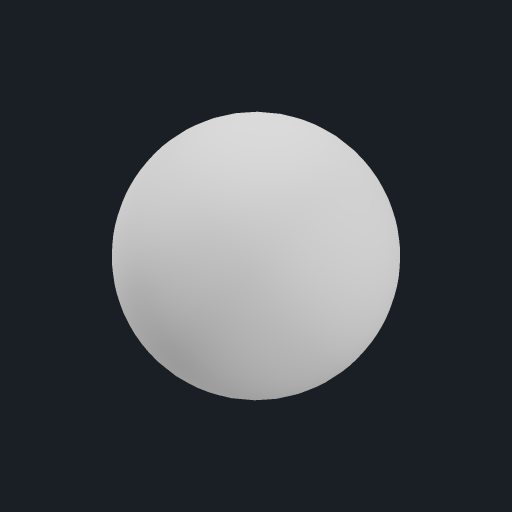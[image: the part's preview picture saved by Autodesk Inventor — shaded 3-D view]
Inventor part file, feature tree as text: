
AUTODESK INVENTOR PART (.ipt)
format: ipt  version: 2023.4 (Build 274418000, 418)  size: 120,320 bytes
history: native  units: in
note: dims shown in document units (in); Inventor stores cm internally (conversion verified against a paired STEP export)
features: revolve x1, sketch x1
ambient origin geometry x8: Origin, YZ Plane, XZ Plane, XY Plane, X Axis, Y Axis, Z Axis, Center Point
bodies: Solid1 (feature_tree)
feature tree (2):
  revolve  "Revolution1"  Angle=90.0deg
  sketch  "Sketch1"  dims[d0=1.1811in d1=90.0deg]
